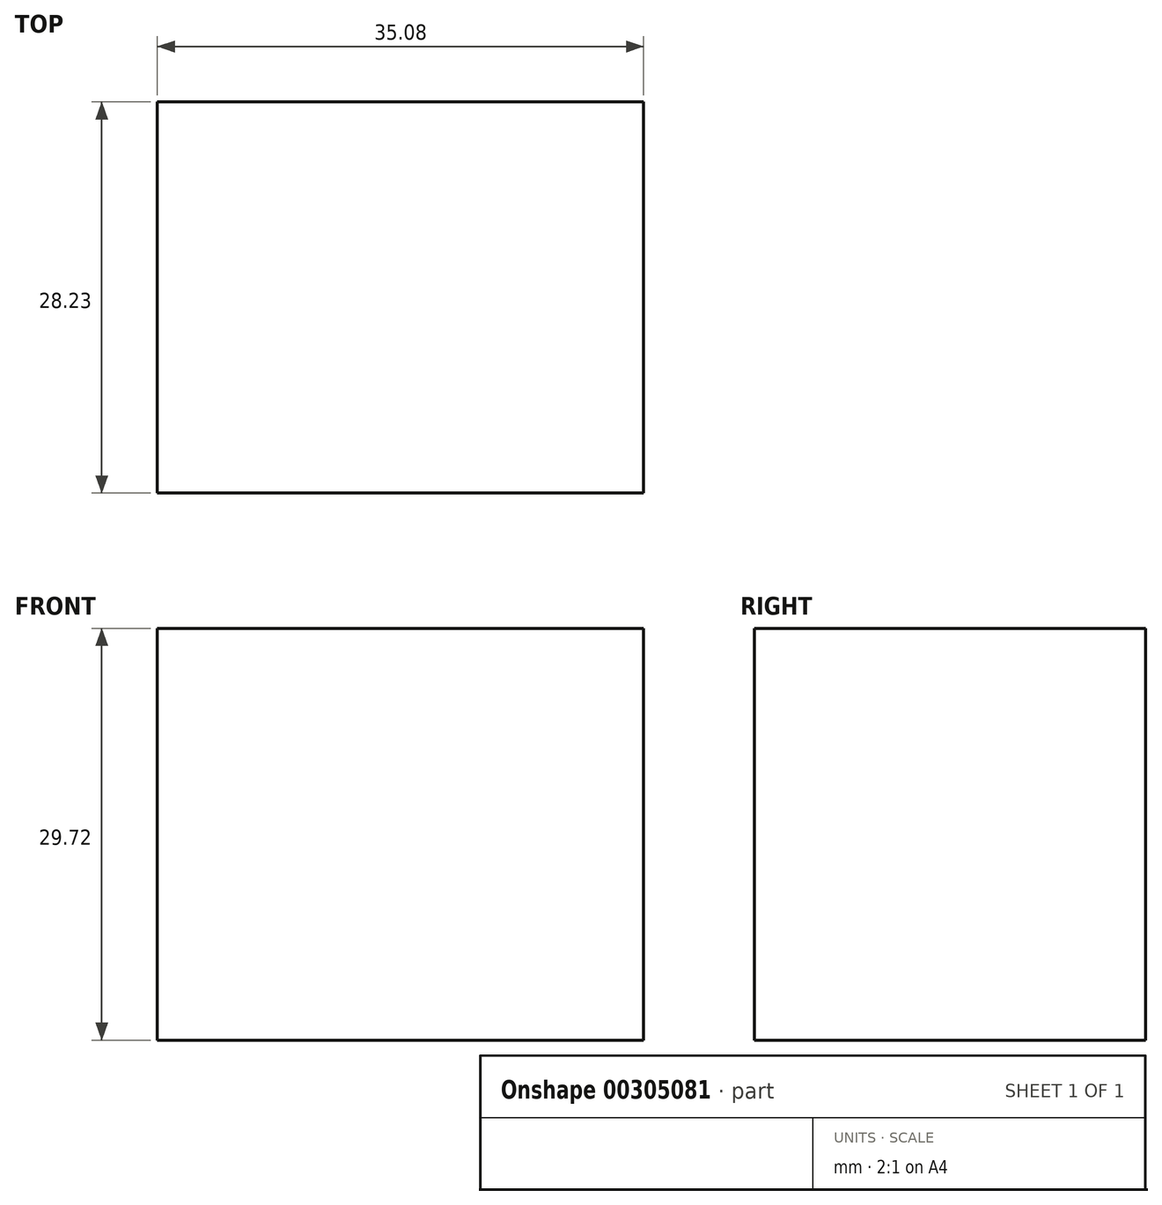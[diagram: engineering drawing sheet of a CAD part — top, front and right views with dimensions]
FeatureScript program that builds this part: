
annotation { "Feature Type Name" : "Feature", "Feature Type Description" : "" }
export const myFeature = defineFeature(function(context is Context, id is Id, definition is map)
    precondition{}
    {
        {
            var Q0;
            Q0=qCreatedBy(makeId("Top.planeOp"),FACE);
            var sketch = newSketch(context, id + "F0", { "sketchPlane" : qUnion([Q0])});
            skLineSegment(sketch, "E0.bottom", {"start": v(0, 28.23) * mm, "end": v(35.08, 28.23) * mm});
            skLineSegment(sketch, "E0.top", {"start": v(0, 0) * mm, "end": v(35.08, 0) * mm});
            skLineSegment(sketch, "E0.left", {"start": v(0, 28.23) * mm, "end": v(0, 0) * mm});
            skLineSegment(sketch, "E0.right", {"start": v(35.08, 28.23) * mm, "end": v(35.08, 0) * mm});
            skSolve(sketch);
        }
        {
            var Q0;
            Q0=makeQuery(id+"F0.imprint","IMPRINT",FACE,{"disambiguationData":[TD([[makeQuery(id+"F0.imprint","IMPRINT",EDGE,{"derivedFrom":sQuery(id+"F0.wireOp",EDGE,"E0.bottom")}),-1.0]])]});
            extrude(context, id + "F1", {"entities" : qUnion([Q0]), "depth" : 29.72 * mm});
        }
    });
